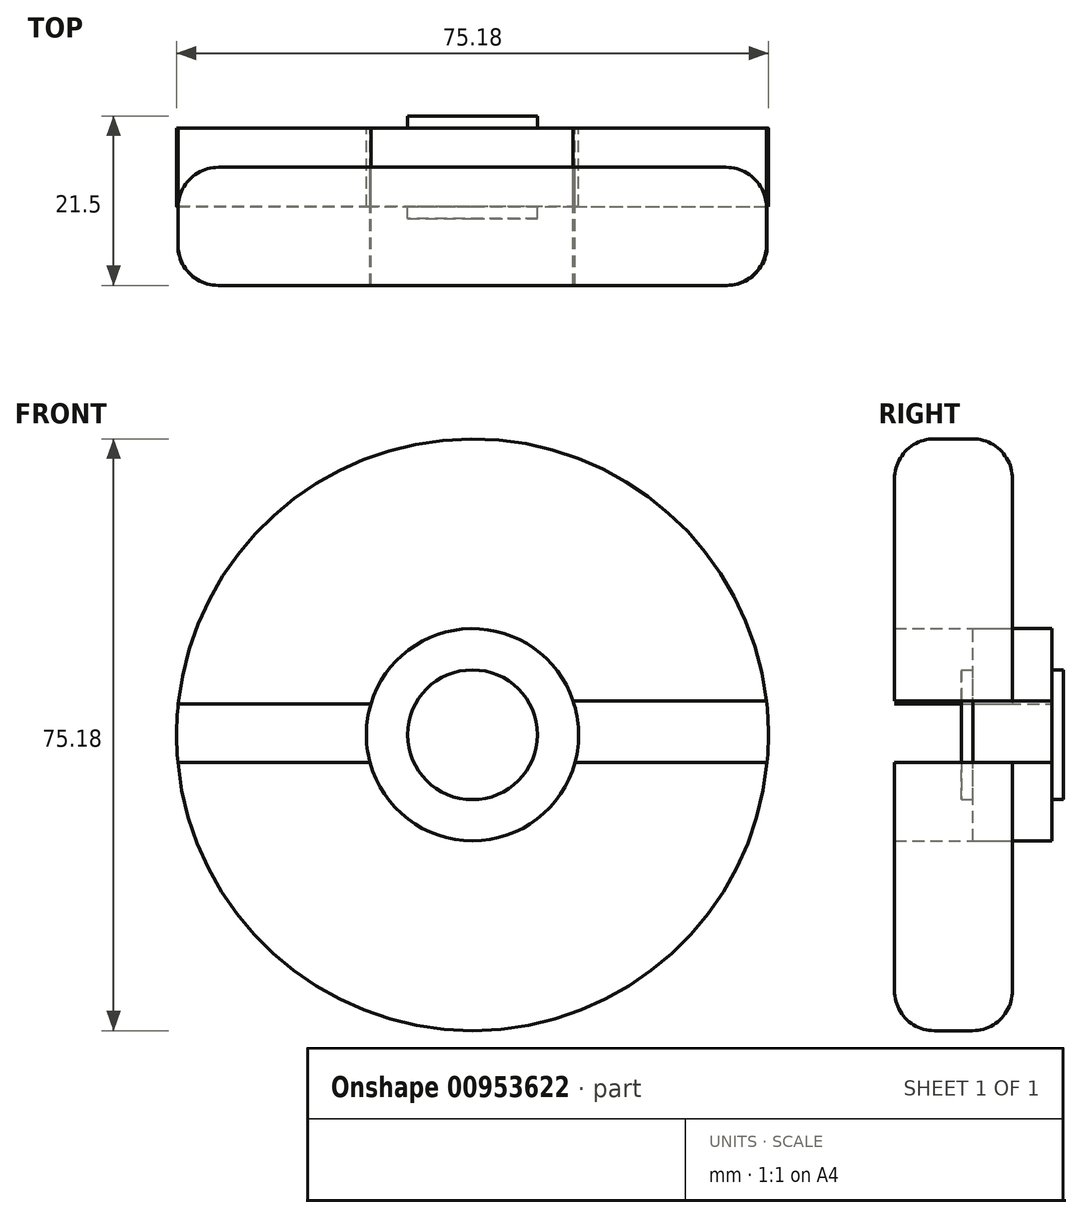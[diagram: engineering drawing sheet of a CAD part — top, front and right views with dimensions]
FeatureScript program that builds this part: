
annotation { "Feature Type Name" : "Feature", "Feature Type Description" : "" }
export const myFeature = defineFeature(function(context is Context, id is Id, definition is map)
    precondition{}
    {
        {
            var Q0;
            Q0=qCreatedBy(makeId("Front.planeOp"),FACE);
            var sketch = newSketch(context, id + "F0", { "sketchPlane" : qUnion([Q0])});
            skCircle(sketch, "E0", {"center": v(0, 0) * mm, "radius": 8.24 * mm});
            skCircle(sketch, "E1", {"center": v(0, 0) * mm, "radius": 13.48 * mm});
            skCircle(sketch, "E2", {"center": v(0, 0) * mm, "radius": 37.59 * mm});
            skLineSegment(sketch, "E3", {"start": v(-12.9, 3.91) * mm, "end": v(-37.38, 3.91) * mm});
            skLineSegment(sketch, "E4", {"start": v(12.77, 4.32) * mm, "end": v(37.34, 4.32) * mm});
            skLineSegment(sketch, "E5", {"start": v(-37.43, -3.49) * mm, "end": v(-13.02, -3.49) * mm});
            skLineSegment(sketch, "E6", {"start": v(13.02, -3.49) * mm, "end": v(37.43, -3.49) * mm});
            skSolve(sketch);
        }
        {
            var Q0;
            {var subQ0=sQuery(id+"F0.wireOp",EDGE,"E5");Q0=makeQuery(id+"F0.imprint","IMPRINT",FACE,{"disambiguationData":[TD([[makeQuery(id+"F0.imprint","IMPRINT",EDGE,{"derivedFrom":subQ0}),-1.0]])]});}
            var Q1;
            {var subQ0=sQuery(id+"F0.wireOp",EDGE,"E3");Q1=makeQuery(id+"F0.imprint","IMPRINT",FACE,{"disambiguationData":[TD([[makeQuery(id+"F0.imprint","IMPRINT",EDGE,{"derivedFrom":subQ0}),-1.0]])]});}
            extrude(context, id + "F1", {"entities" : qUnion([Q0, Q1]), "depth" : 15 * mm, "offsetDistance" : 25.4 * mm});
        }
        {
            var Q0;
            Q0=makeQuery(id+"F0.imprint","IMPRINT",FACE,{"disambiguationData":[TD([[makeQuery(id+"F0.imprint","IMPRINT",EDGE,{"derivedFrom":sQuery(id+"F0.wireOp",EDGE,"E0")}),-1.0]])]});
            extrude(context, id + "F2", {"entities" : qUnion([Q0]), "endBound" : BoundingType.SYMMETRIC, "depth" : 10 * mm, "offsetDistance" : 25.4 * mm});
        }
        {
            var Q0;
            Q0=makeQuery(id+"F0.imprint","IMPRINT",FACE,{"disambiguationData":[TD([[makeQuery(id+"F0.imprint","IMPRINT",EDGE,{"derivedFrom":sQuery(id+"F0.wireOp",EDGE,"E0")}),1.0]])]});
            extrude(context, id + "F3", {"entities" : qUnion([Q0]), "operationType" : NewBodyOperationType.ADD, "endBound" : BoundingType.SYMMETRIC, "depth" : 13 * mm, "offsetDistance" : 25.4 * mm});
        }
        {
            var Q0;
            {var subQ1=sQuery(id+"F0.wireOp",EDGE,"E3");Q0=makeQuery(id+"F0.imprint","IMPRINT",FACE,{"disambiguationData":[TD([[makeQuery(id+"F0.imprint","IMPRINT",EDGE,{"derivedFrom":subQ1}),1.0]])]});}
            var Q1;
            {var subQ0=sQuery(id+"F0.wireOp",EDGE,"E4");Q1=makeQuery(id+"F0.imprint","IMPRINT",FACE,{"disambiguationData":[TD([[makeQuery(id+"F0.imprint","IMPRINT",EDGE,{"derivedFrom":subQ0}),-1.0]])]});}
            extrude(context, id + "F4", {"entities" : qUnion([Q0, Q1]), "endBound" : BoundingType.SYMMETRIC, "depth" : 10 * mm, "offsetDistance" : 25.4 * mm});
        }
        {
            var Q0;
            {var subQ0=sQuery(id+"F0.wireOp",EDGE,"E2");Q0=makeQuery(id+"F1.opExtrude","CAP_EDGE",EDGE,{"disambiguationData":[OSD([subQ0]),TDD([makeQuery(id+"F0.imprint","IMPRINT",EDGE,{"disambiguationData":[TD([[makeQuery(id+"F0.imprint","INTERSECT",VERTEX,{"derivedFrom":[subQ0,sQuery(id+"F0.wireOp",EDGE,"E3")]}),1.0]])],"derivedFrom":subQ0})])],"isStart":false});}
            var Q1;
            {var subQ0=sQuery(id+"F0.wireOp",EDGE,"E2");Q1=makeQuery(id+"F1.opExtrude","CAP_EDGE",EDGE,{"disambiguationData":[OSD([subQ0]),TDD([makeQuery(id+"F0.imprint","IMPRINT",EDGE,{"disambiguationData":[TD([[makeQuery(id+"F0.imprint","INTERSECT",VERTEX,{"derivedFrom":[subQ0,sQuery(id+"F0.wireOp",EDGE,"E3")]}),1.0]])],"derivedFrom":subQ0})])],"isStart":true});}
            var Q2;
            {var subQ0=sQuery(id+"F0.wireOp",EDGE,"E2");Q2=makeQuery(id+"F1.opExtrude","CAP_EDGE",EDGE,{"disambiguationData":[OSD([subQ0]),TDD([makeQuery(id+"F0.imprint","IMPRINT",EDGE,{"disambiguationData":[TD([[makeQuery(id+"F0.imprint","INTERSECT",VERTEX,{"derivedFrom":[subQ0,sQuery(id+"F0.wireOp",EDGE,"E5")]}),-1.0]])],"derivedFrom":subQ0})])],"isStart":false});}
            var Q3;
            {var subQ0=sQuery(id+"F0.wireOp",EDGE,"E2");Q3=makeQuery(id+"F1.opExtrude","CAP_EDGE",EDGE,{"disambiguationData":[OSD([subQ0]),TDD([makeQuery(id+"F0.imprint","IMPRINT",EDGE,{"disambiguationData":[TD([[makeQuery(id+"F0.imprint","INTERSECT",VERTEX,{"derivedFrom":[subQ0,sQuery(id+"F0.wireOp",EDGE,"E5")]}),-1.0]])],"derivedFrom":subQ0})])],"isStart":true});}
            fillet(context, id + "F5", {"entities" : qUnion([Q0, Q1, Q2, Q3]), "radius" : 5.08 * mm, "tangentPropagation" : true, "allowEdgeOverflow" : false});
        }
    });
